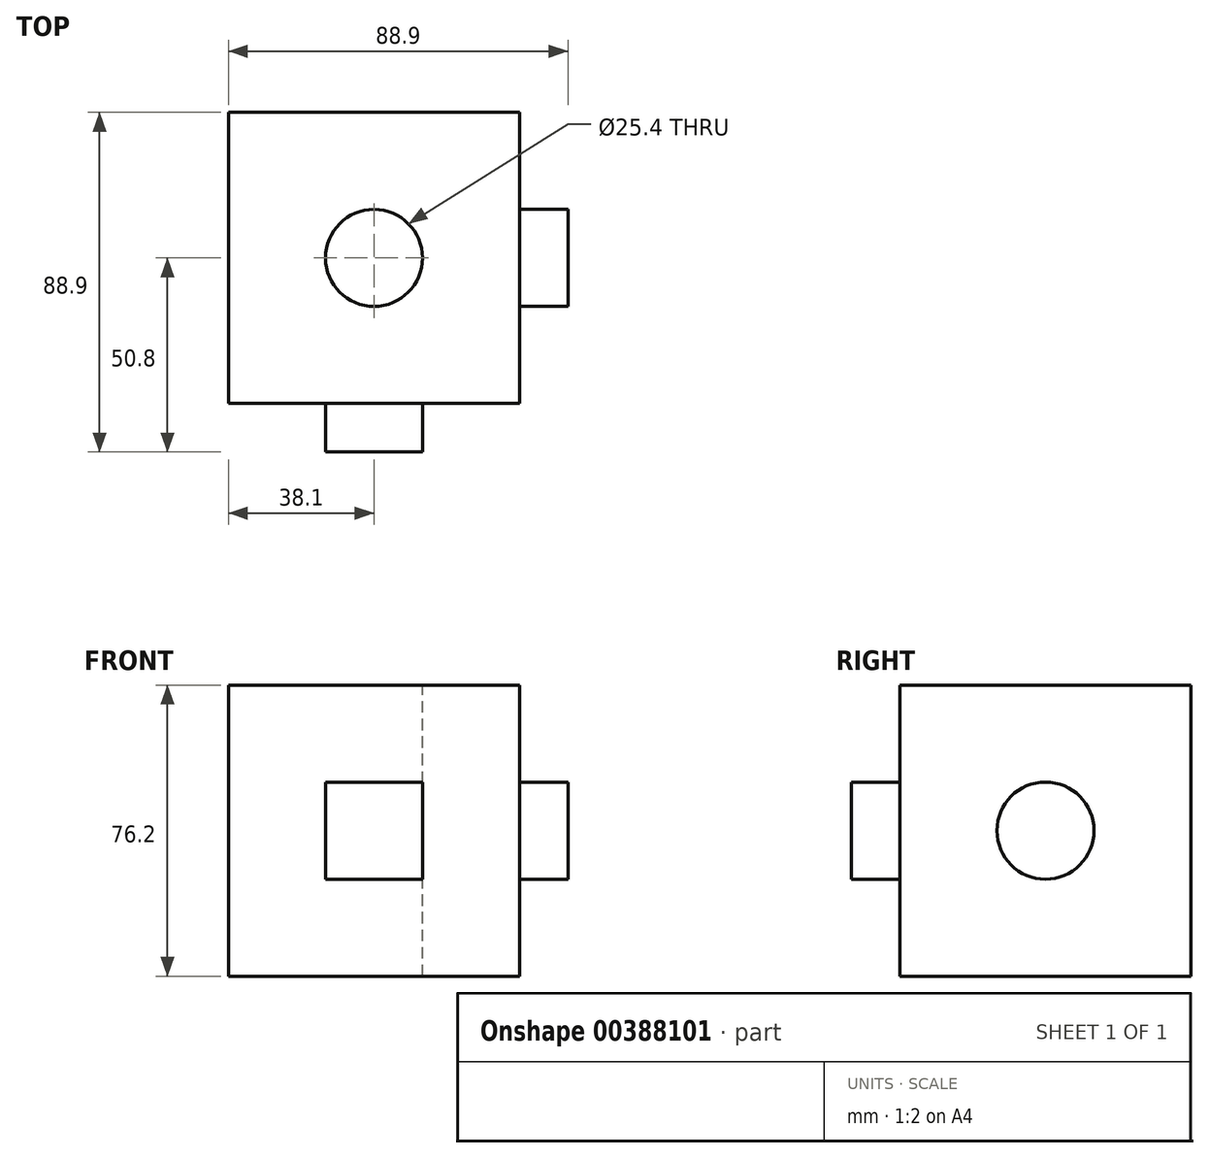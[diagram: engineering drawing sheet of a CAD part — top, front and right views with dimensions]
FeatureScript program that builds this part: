
annotation { "Feature Type Name" : "Feature", "Feature Type Description" : "" }
export const myFeature = defineFeature(function(context is Context, id is Id, definition is map)
    precondition{}
    {
        {
            var Q0;
            Q0=qCreatedBy(makeId("Front.planeOp"),FACE);
            var sketch = newSketch(context, id + "F0", { "sketchPlane" : qUnion([Q0])});
            skLineSegment(sketch, "E0.bottom", {"start": v(-76.2, 76.2) * mm, "end": v(0, 76.2) * mm});
            skLineSegment(sketch, "E0.top", {"start": v(-76.2, 0) * mm, "end": v(0, 0) * mm});
            skLineSegment(sketch, "E0.left", {"start": v(-76.2, 76.2) * mm, "end": v(-76.2, 0) * mm});
            skLineSegment(sketch, "E0.right", {"start": v(0, 76.2) * mm, "end": v(0, 0) * mm});
            skSolve(sketch);
        }
        {
            var Q0;
            Q0=makeQuery(id+"F0.imprint","IMPRINT",FACE,{"disambiguationData":[TD([[makeQuery(id+"F0.imprint","IMPRINT",EDGE,{"derivedFrom":sQuery(id+"F0.wireOp",EDGE,"E0.bottom")}),-1.0]])]});
            extrude(context, id + "F1", {"entities" : qUnion([Q0]), "depth" : 76.2 * mm});
        }
        {
            var Q0;
            Q0=makeQuery(id+"F1.opExtrude","SWEPT_FACE",FACE,{"disambiguationData":[OSD([sQuery(id+"F0.wireOp",EDGE,"E0.bottom")])]});
            var sketch = newSketch(context, id + "F2", { "sketchPlane" : qUnion([Q0])});
            skPoint(sketch, "E1", {"position": v(-38.1, -38.1) * mm});
            skSolve(sketch);
        }
        {
            var Q0;
            Q0=sQuery(id+"F2.wireOp",VERTEX,"E1");
            var Q1;
            Q1=makeQuery(id+"F1.opExtrude","SWEPT_BODY",BODY,{"disambiguationData":[OSD([sQuery(id+"F0.wireOp",EDGE,"E0.bottom"),sQuery(id+"F0.wireOp",EDGE,"E0.top"),sQuery(id+"F0.wireOp",EDGE,"E0.left"),sQuery(id+"F0.wireOp",EDGE,"E0.right")])]});
            hole(context, id + "F3", {"style" : HoleStyle.SIMPLE, "endStyle" : HoleEndStyle.THROUGH, "holeDiameter" : 25.4 * mm, "isTappedThrough" : true, "tappedDepth" : 12.7 * mm, "tapClearance" : 3, "locations" : qUnion([Q0]), "scope" : qUnion([Q1])});
        }
        {
            var Q0;
            Q0=makeQuery(id+"F1.opExtrude","CAP_FACE",FACE,{"disambiguationData":[OSD([sQuery(id+"F0.wireOp",EDGE,"E0.bottom"),sQuery(id+"F0.wireOp",EDGE,"E0.top"),sQuery(id+"F0.wireOp",EDGE,"E0.left"),sQuery(id+"F0.wireOp",EDGE,"E0.right")])],"isStart":false});
            var sketch = newSketch(context, id + "F4", { "sketchPlane" : qUnion([Q0])});
            skLineSegment(sketch, "E2.bottom", {"start": v(-50.8, 50.8) * mm, "end": v(-25.4, 50.8) * mm});
            skLineSegment(sketch, "E2.top", {"start": v(-50.8, 25.4) * mm, "end": v(-25.4, 25.4) * mm});
            skLineSegment(sketch, "E2.left", {"start": v(-50.8, 50.8) * mm, "end": v(-50.8, 25.4) * mm});
            skLineSegment(sketch, "E2.right", {"start": v(-25.4, 50.8) * mm, "end": v(-25.4, 25.4) * mm});
            skSolve(sketch);
        }
        {
            var Q0;
            Q0=makeQuery(id+"F4.imprint","IMPRINT",FACE,{"disambiguationData":[TD([[makeQuery(id+"F4.imprint","IMPRINT",EDGE,{"derivedFrom":sQuery(id+"F4.wireOp",EDGE,"E2.bottom")}),-1.0]])]});
            extrude(context, id + "F5", {"entities" : qUnion([Q0]), "operationType" : NewBodyOperationType.ADD, "depth" : 12.7 * mm});
        }
        {
            var Q0;
            Q0=makeQuery(id+"F1.opExtrude","SWEPT_FACE",FACE,{"disambiguationData":[OSD([sQuery(id+"F0.wireOp",EDGE,"E0.right")])]});
            var sketch = newSketch(context, id + "F6", { "sketchPlane" : qUnion([Q0])});
            skPoint(sketch, "E3", {"position": v(-38.1, 38.1) * mm});
            skCircle(sketch, "E4", {"center": v(-38.1, 38.1) * mm, "radius": 12.7 * mm});
            skSolve(sketch);
        }
        {
            var Q0;
            Q0=makeQuery(id+"F6.imprint","IMPRINT",FACE,{"disambiguationData":[TD([[makeQuery(id+"F6.imprint","IMPRINT",EDGE,{"derivedFrom":sQuery(id+"F6.wireOp",EDGE,"E4")}),1.0]])]});
            extrude(context, id + "F7", {"entities" : qUnion([Q0]), "operationType" : NewBodyOperationType.ADD, "depth" : 12.7 * mm});
        }
    });
